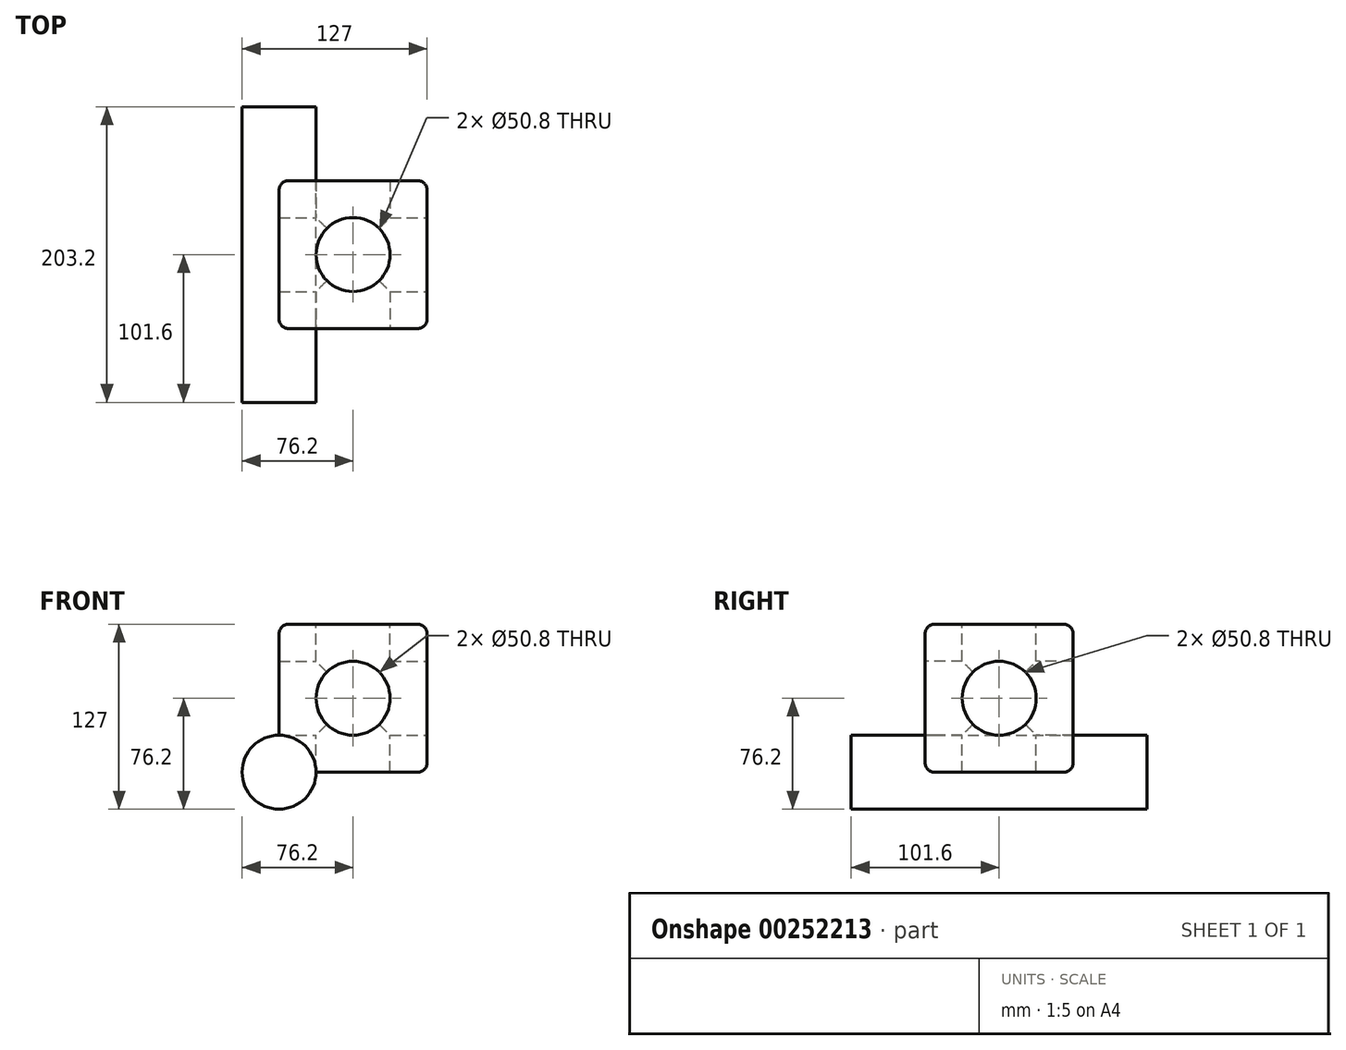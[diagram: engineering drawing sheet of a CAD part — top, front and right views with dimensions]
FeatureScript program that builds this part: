
annotation { "Feature Type Name" : "Feature", "Feature Type Description" : "" }
export const myFeature = defineFeature(function(context is Context, id is Id, definition is map)
    precondition{}
    {
        {
            var Q0;
            Q0=qCreatedBy(makeId("Front.planeOp"),FACE);
            var sketch = newSketch(context, id + "F0", { "sketchPlane" : qUnion([Q0])});
            skLineSegment(sketch, "E0", {"start": v(0, 0) * mm, "end": v(101.6, 0) * mm});
            skLineSegment(sketch, "E1", {"start": v(101.6, 0) * mm, "end": v(101.6, 101.6) * mm});
            skLineSegment(sketch, "E2", {"start": v(101.6, 101.6) * mm, "end": v(0, 101.6) * mm});
            skLineSegment(sketch, "E3", {"start": v(0, 101.6) * mm, "end": v(0, 0) * mm});
            skSolve(sketch);
        }
        {
            var Q0;
            Q0=makeQuery(id+"F0.imprint","IMPRINT",FACE,{"disambiguationData":[TD([[makeQuery(id+"F0.imprint","IMPRINT",EDGE,{"derivedFrom":sQuery(id+"F0.wireOp",EDGE,"E0")}),1.0]])]});
            extrude(context, id + "F1", {"entities" : qUnion([Q0]), "depth" : 101.6 * mm});
        }
        {
            var Q0;
            Q0=makeQuery(id+"F1.opExtrude","SWEPT_FACE",FACE,{"disambiguationData":[OSD([sQuery(id+"F0.wireOp",EDGE,"E2")])]});
            var sketch = newSketch(context, id + "F2", { "sketchPlane" : qUnion([Q0])});
            skCircle(sketch, "E4", {"center": v(50.8, -50.8) * mm, "radius": 25.4 * mm});
            skPoint(sketch, "E5.orphan", {"position": v(50.8, 0) * mm});
            skPoint(sketch, "E6.end.orphan", {"position": v(50.8, -101.6) * mm});
            skSolve(sketch);
        }
        {
            var Q0;
            Q0=makeQuery(id+"F2.imprint","IMPRINT",FACE,{"disambiguationData":[TD([[makeQuery(id+"F2.imprint","IMPRINT",EDGE,{"derivedFrom":sQuery(id+"F2.wireOp",EDGE,"E4")}),1.0]])]});
            extrude(context, id + "F3", {"entities" : qUnion([Q0]), "operationType" : NewBodyOperationType.REMOVE, "oppositeDirection" : true, "depth" : 101.6 * mm});
        }
        {
            var Q0;
            Q0=makeQuery(id+"F1.opExtrude","CAP_FACE",FACE,{"disambiguationData":[OSD([sQuery(id+"F0.wireOp",EDGE,"E0"),sQuery(id+"F0.wireOp",EDGE,"E1"),sQuery(id+"F0.wireOp",EDGE,"E2"),sQuery(id+"F0.wireOp",EDGE,"E3")])],"isStart":false});
            var sketch = newSketch(context, id + "F4", { "sketchPlane" : qUnion([Q0])});
            skCircle(sketch, "E7", {"center": v(50.8, 50.8) * mm, "radius": 25.4 * mm});
            skPoint(sketch, "E8.orphan", {"position": v(50.8, 101.6) * mm});
            skPoint(sketch, "E9.end.orphan", {"position": v(50.8, 0) * mm});
            skSolve(sketch);
        }
        {
            var Q0;
            Q0=makeQuery(id+"F4.imprint","IMPRINT",FACE,{"disambiguationData":[TD([[makeQuery(id+"F4.imprint","IMPRINT",EDGE,{"derivedFrom":sQuery(id+"F4.wireOp",EDGE,"E7")}),1.0]])]});
            extrude(context, id + "F5", {"entities" : qUnion([Q0]), "operationType" : NewBodyOperationType.REMOVE, "oppositeDirection" : true, "depth" : 101.6 * mm});
        }
        {
            var Q0;
            Q0=makeQuery(id+"F1.opExtrude","SWEPT_FACE",FACE,{"disambiguationData":[OSD([sQuery(id+"F0.wireOp",EDGE,"E1")])]});
            var sketch = newSketch(context, id + "F6", { "sketchPlane" : qUnion([Q0])});
            skCircle(sketch, "E10", {"center": v(-50.8, 50.8) * mm, "radius": 25.4 * mm});
            skPoint(sketch, "E11.orphan", {"position": v(-50.8, 101.6) * mm});
            skPoint(sketch, "E12.end.orphan", {"position": v(-50.8, 0) * mm});
            skSolve(sketch);
        }
        {
            var Q0;
            Q0=makeQuery(id+"F6.imprint","IMPRINT",FACE,{"disambiguationData":[TD([[makeQuery(id+"F6.imprint","IMPRINT",EDGE,{"derivedFrom":sQuery(id+"F6.wireOp",EDGE,"E10")}),1.0]])]});
            extrude(context, id + "F7", {"entities" : qUnion([Q0]), "operationType" : NewBodyOperationType.REMOVE, "oppositeDirection" : true, "depth" : 101.6 * mm});
        }
        {
            var Q0;
            Q0=makeQuery(id+"F1.opExtrude","CAP_EDGE",EDGE,{"disambiguationData":[OSD([sQuery(id+"F0.wireOp",EDGE,"E2")])],"isStart":false});
            var Q1;
            Q1=makeQuery(id+"F1.opExtrude","SWEPT_EDGE",EDGE,{"disambiguationData":[OSD([sQuery(id+"F0.wireOp",EDGE,"E2"),sQuery(id+"F0.wireOp",EDGE,"E3")])]});
            var Q2;
            Q2=makeQuery(id+"F1.opExtrude","CAP_EDGE",EDGE,{"disambiguationData":[OSD([sQuery(id+"F0.wireOp",EDGE,"E2")])],"isStart":true});
            var Q3;
            Q3=makeQuery(id+"F1.opExtrude","SWEPT_EDGE",EDGE,{"disambiguationData":[OSD([sQuery(id+"F0.wireOp",EDGE,"E1"),sQuery(id+"F0.wireOp",EDGE,"E2")])]});
            var Q4;
            Q4=makeQuery(id+"F1.opExtrude","CAP_EDGE",EDGE,{"disambiguationData":[OSD([sQuery(id+"F0.wireOp",EDGE,"E3")])],"isStart":false});
            var Q5;
            Q5=makeQuery(id+"F1.opExtrude","CAP_EDGE",EDGE,{"disambiguationData":[OSD([sQuery(id+"F0.wireOp",EDGE,"E1")])],"isStart":false});
            var Q6;
            Q6=makeQuery(id+"F1.opExtrude","CAP_EDGE",EDGE,{"disambiguationData":[OSD([sQuery(id+"F0.wireOp",EDGE,"E0")])],"isStart":false});
            var Q7;
            Q7=makeQuery(id+"F1.opExtrude","SWEPT_EDGE",EDGE,{"disambiguationData":[OSD([sQuery(id+"F0.wireOp",EDGE,"E0"),sQuery(id+"F0.wireOp",EDGE,"E1")])]});
            var Q8;
            Q8=makeQuery(id+"F1.opExtrude","CAP_EDGE",EDGE,{"disambiguationData":[OSD([sQuery(id+"F0.wireOp",EDGE,"E1")])],"isStart":true});
            var Q9;
            Q9=makeQuery(id+"F1.opExtrude","CAP_EDGE",EDGE,{"disambiguationData":[OSD([sQuery(id+"F0.wireOp",EDGE,"E3")])],"isStart":true});
            var Q10;
            Q10=makeQuery(id+"F1.opExtrude","CAP_EDGE",EDGE,{"disambiguationData":[OSD([sQuery(id+"F0.wireOp",EDGE,"E0")])],"isStart":true});
            var Q11;
            Q11=makeQuery(id+"F1.opExtrude","SWEPT_EDGE",EDGE,{"disambiguationData":[OSD([sQuery(id+"F0.wireOp",EDGE,"E0"),sQuery(id+"F0.wireOp",EDGE,"E3")])]});
            fillet(context, id + "F8", {"entities" : qUnion([Q0, Q1, Q2, Q3, Q4, Q5, Q6, Q7, Q8, Q9, Q10, Q11]), "radius" : 6.35 * mm, "tangentPropagation" : true, "allowEdgeOverflow" : false});
        }
        {
            var Q0;
            Q0=qCreatedBy(makeId("Front.planeOp"),FACE);
            cPlane(context, id + "F9", {"entities" : qUnion([Q0]), "cplaneType" : CPlaneType.OFFSET, "offset" : 101.6 * mm, "width" : 152.4 * mm, "height" : 152.4 * mm});
        }
        {
            var Q0;
            Q0=qCreatedBy(id+"F9.planeOp",FACE);
            var sketch = newSketch(context, id + "F10", { "sketchPlane" : qUnion([Q0])});
            skCircle(sketch, "E13", {"center": v(0, 0) * mm, "radius": 25.4 * mm});
            skSolve(sketch);
        }
        {
            var Q0;
            Q0 = qSketchRegion(id + "F10", true);
            extrude(context, id + "F11", {"entities" : qUnion([Q0]), "operationType" : NewBodyOperationType.ADD, "depth" : 50.8 * mm, "hasSecondDirection" : true, "secondDirectionOppositeDirection" : true, "secondDirectionDepth" : 152.4 * mm});
        }
    });
